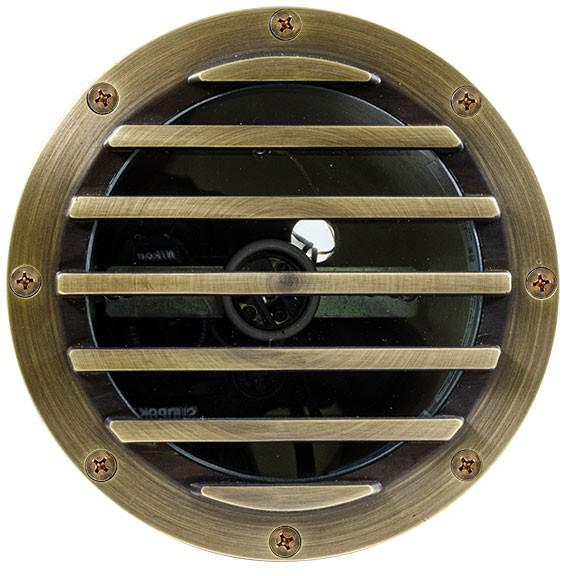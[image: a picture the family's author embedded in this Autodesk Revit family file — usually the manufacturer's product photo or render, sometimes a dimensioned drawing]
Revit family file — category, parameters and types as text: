
# Revit family: Alcon-9150-S90-Revit-Family
name_source: partatom
category: Luminarias
units: mm (PartAtom-declared; Revit-internal decimal feet)

## family parameters
Anfitrión = Cara
Compartido = No
Corte con vacíos al cargar = No
Cota de conector redondo = Usar diámetro
Mantener orientación de anotación = No
Origen de luz = Sí
Punto de cálculo de habitación = No
Tipo de pieza = Normal

## types (1)
- Alcon-9150-S90-Revit-Family
    Cambio de temperatura de color de luz atenuada = <Ninguno>
    Elevación por defecto = 4' - 0"
    Fabricante = Alcon Lighting
    Filtro de color = 16777215
    GLASS LENS = Analytical Panels
    HOUSING = <Por categoría>
    LENS GLASS = Glass
    Link to IES File = https://www.alconlighting.com
    Longitud de símbolo de origen de luz = 10' - 0"
    Modelo = Alcon Lighting 9150-S90
    Product Data URL = https://www.alconlighting.com
    Product Page = https://www.alconlighting.com
    TAP LENS = <Por categoría>
    TOP FINISH = <Por categoría>
    URL = https://www.alconlighting.com
    Ángulo de campo de foco = 90.00°
    Ángulo de enfoque = 30.00°
    Ángulo de inclinación = 60.00°

## geometry (parser evidence)
native form markers: Sweep x3
no freeform markers — native parametric forms only
